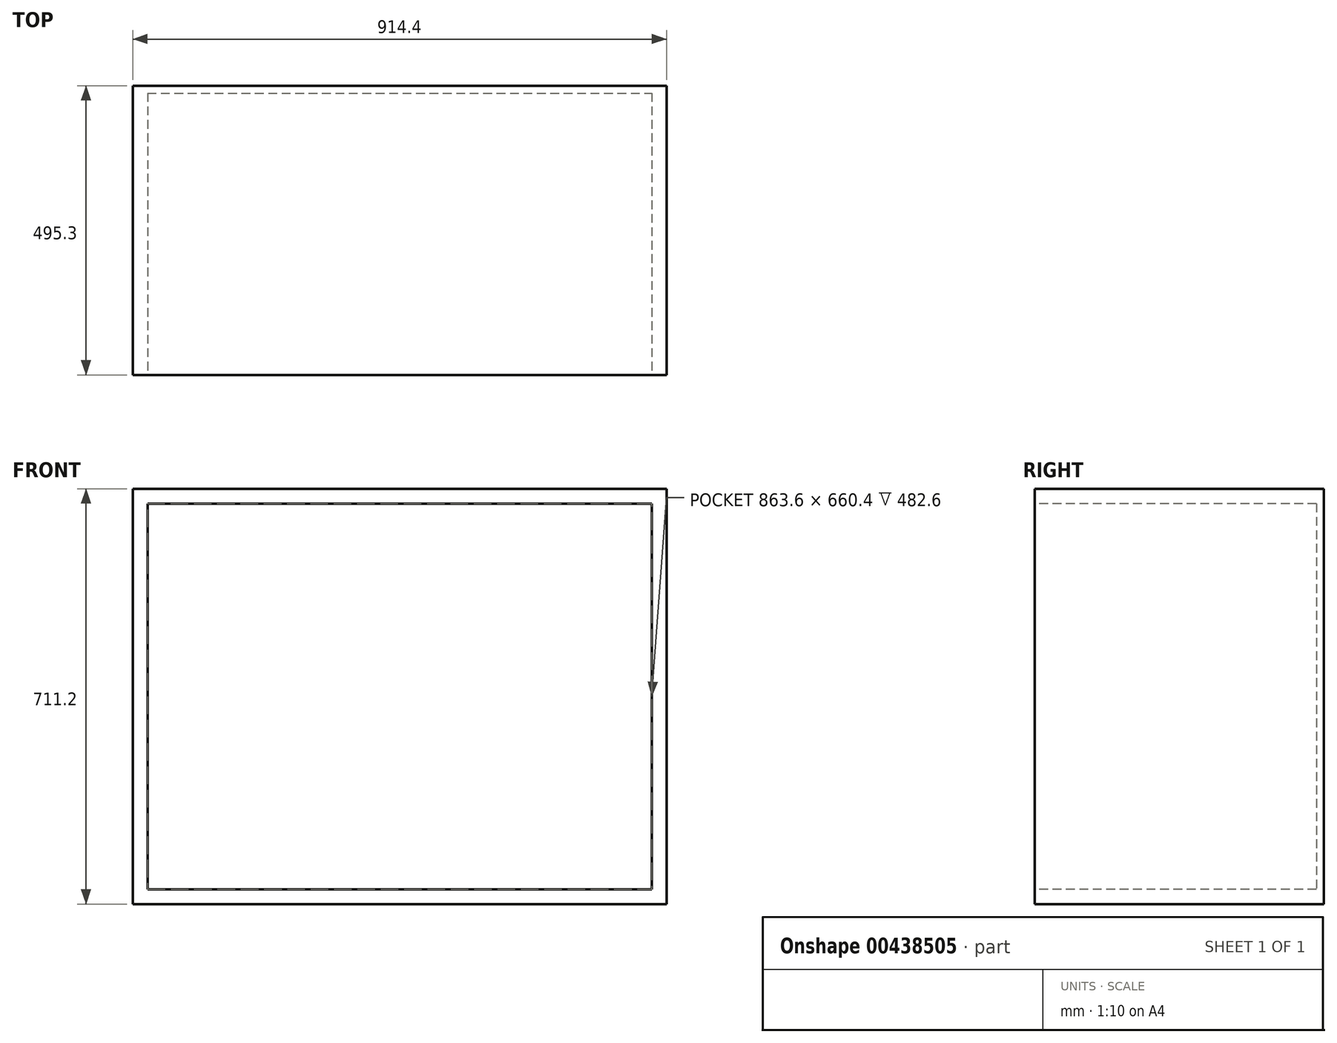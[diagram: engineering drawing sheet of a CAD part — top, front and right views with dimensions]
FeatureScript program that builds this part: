
annotation { "Feature Type Name" : "Feature", "Feature Type Description" : "" }
export const myFeature = defineFeature(function(context is Context, id is Id, definition is map)
    precondition{}
    {
        {
            var Q0;
            Q0=qCreatedBy(makeId("Top.planeOp"),FACE);
            var sketch = newSketch(context, id + "F0", { "sketchPlane" : qUnion([Q0])});
            skLineSegment(sketch, "E0.bottom", {"start": v(0, 0) * mm, "end": v(914.4, 0) * mm});
            skLineSegment(sketch, "E0.top", {"start": v(0, -495.3) * mm, "end": v(914.4, -495.3) * mm});
            skLineSegment(sketch, "E0.left", {"start": v(0, 0) * mm, "end": v(0, -495.3) * mm});
            skLineSegment(sketch, "E0.right", {"start": v(914.4, 0) * mm, "end": v(914.4, -495.3) * mm});
            skSolve(sketch);
        }
        {
            var Q0;
            Q0 = qSketchRegion(id + "F0", true);
            extrude(context, id + "F1", {"entities" : qUnion([Q0]), "depth" : 711.2 * mm});
        }
        {
            var Q0;
            Q0=makeQuery(id+"F1.opExtrude","SWEPT_FACE",FACE,{"disambiguationData":[OSD([sQuery(id+"F0.wireOp",EDGE,"E0.top")])]});
            var sketch = newSketch(context, id + "F2", { "sketchPlane" : qUnion([Q0])});
            skLineSegment(sketch, "E1.0", {"start": v(25.4, 25.4) * mm, "end": v(889, 25.4) * mm});
            skLineSegment(sketch, "E1.1", {"start": v(25.4, 685.8) * mm, "end": v(25.4, 25.4) * mm});
            skLineSegment(sketch, "E1.2", {"start": v(889, 685.8) * mm, "end": v(25.4, 685.8) * mm});
            skLineSegment(sketch, "E1.3", {"start": v(889, 25.4) * mm, "end": v(889, 685.8) * mm});
            skSolve(sketch);
        }
        {
            var Q0;
            Q0 = qSketchRegion(id + "F2", true);
            extrude(context, id + "F3", {"entities" : qUnion([Q0]), "operationType" : NewBodyOperationType.REMOVE, "oppositeDirection" : true, "depth" : 482.6 * mm});
        }
    });
